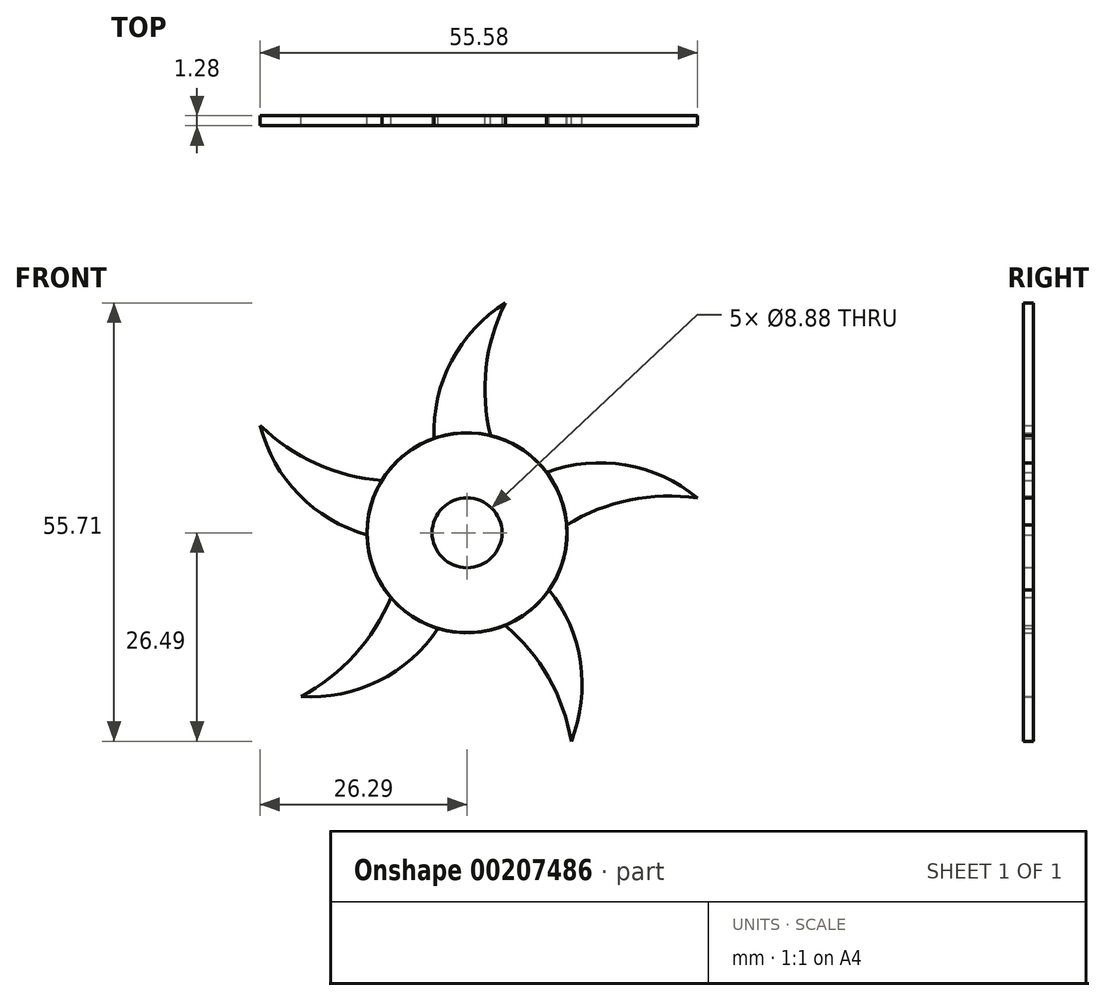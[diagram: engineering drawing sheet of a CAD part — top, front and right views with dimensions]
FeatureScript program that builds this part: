
annotation { "Feature Type Name" : "Feature", "Feature Type Description" : "" }
export const myFeature = defineFeature(function(context is Context, id is Id, definition is map)
    precondition{}
    {
        {
            var Q0;
            Q0=qCreatedBy(makeId("Front.planeOp"),FACE);
            var sketch = newSketch(context, id + "F0", { "sketchPlane" : qUnion([Q0])});
            skCircle(sketch, "E0", {"center": v(0, 0) * mm, "radius": 12.7 * mm});
            skSolve(sketch);
        }
        {
            var Q0;
            Q0=qSketchRegion(id+"F0",true);
            extrude(context, id + "F1", {"entities" : qUnion([Q0]), "endBound" : BoundingType.SYMMETRIC, "depth" : 1.27 * mm});
        }
        {
            var Q0;
            Q0=qCreatedBy(makeId("Front.planeOp"),FACE);
            var sketch = newSketch(context, id + "F2", { "sketchPlane" : qUnion([Q0])});
            skLineSegment(sketch, "E1.top", {"start": v(3.9, 9.4) * mm, "end": v(-3.9, 9.4) * mm});
            skPoint(sketch, "E1.middle", {"position": v(0, 12.38) * mm});
            skArc(sketch, "E2", {"start": v(4.86, 29.22) * mm, "mid": v(2.3, 19.4) * mm, "end": v(3.9, 9.4) * mm});
            skArc(sketch, "E3", {"start": v(4.86, 29.22) * mm, "mid": v(-2.54, 20.64) * mm, "end": v(-3.9, 9.4) * mm});
            skSolve(sketch);
        }
        {
            var Q0;
            Q0=qSketchRegion(id+"F2",true);
            extrude(context, id + "F3", {"entities" : qUnion([Q0]), "operationType" : NewBodyOperationType.ADD, "endBound" : BoundingType.SYMMETRIC, "depth" : 1.27 * mm});
        }
        {
            var Q0;
            Q0=makeQuery(id+"F1.opExtrude","SWEPT_BODY",BODY,{"disambiguationData":[OSD([sQuery(id+"F0.wireOp",EDGE,"E0")])]});
            var Q1;
            Q1=sQuery(id+"F0.wireOp",EDGE,"E0");
            circularPattern(context, id + "F4", {"entities" : qUnion([Q0]), "axis" : qUnion([Q1]), "angle" : 360 * degree, "instanceCount" : 5, "equalSpace" : true});
        }
        {
            var Q0;
            Q0=qCreatedBy(makeId("Front.planeOp"),FACE);
            var sketch = newSketch(context, id + "F5", { "sketchPlane" : qUnion([Q0])});
            skCircle(sketch, "E4", {"center": v(0, 0) * mm, "radius": 4.44 * mm});
            skSolve(sketch);
        }
        {
            var Q0;
            Q0=qSketchRegion(id+"F5",true);
            extrude(context, id + "F6", {"entities" : qUnion([Q0]), "operationType" : NewBodyOperationType.REMOVE, "endBound" : BoundingType.SYMMETRIC, "oppositeDirection" : true, "depth" : 1.27 * mm});
        }
    });
